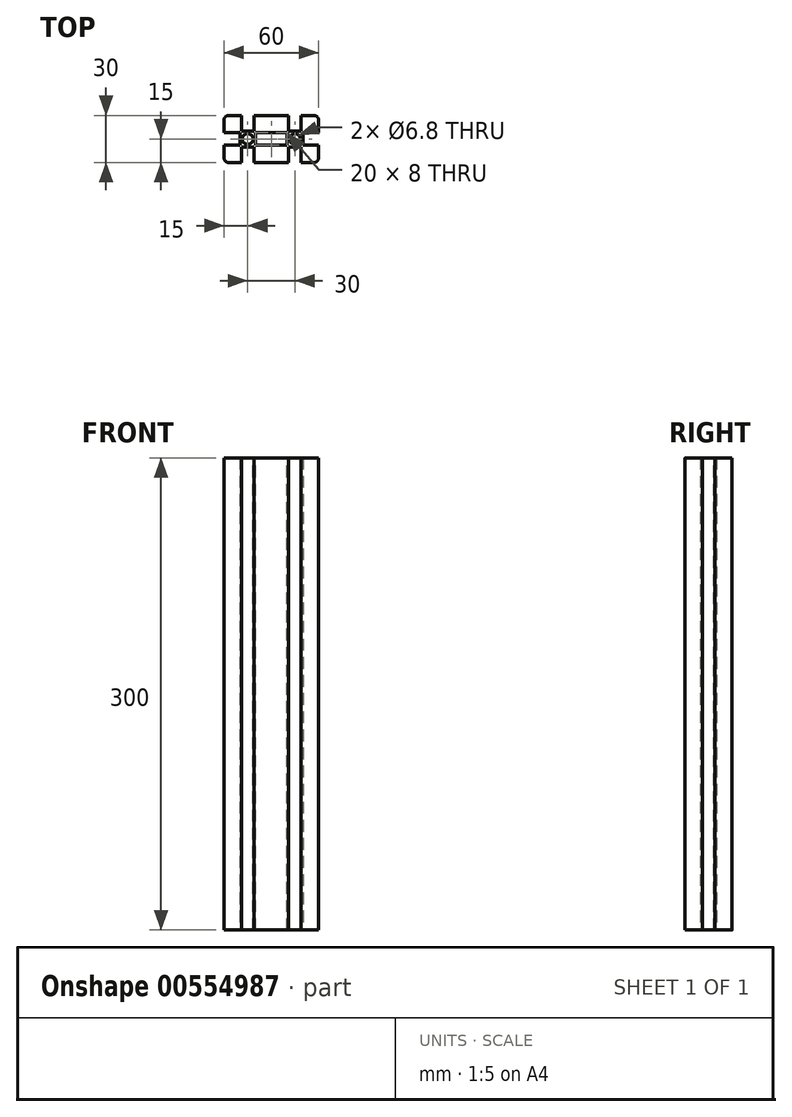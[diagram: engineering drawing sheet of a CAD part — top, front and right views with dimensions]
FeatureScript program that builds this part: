
annotation { "Feature Type Name" : "Feature", "Feature Type Description" : "" }
export const myFeature = defineFeature(function(context is Context, id is Id, definition is map)
    precondition{}
    {
        {
            var Q0;
            Q0=qCreatedBy(makeId("Top.planeOp"),FACE);
            var sketch = newSketch(context, id + "F0", { "sketchPlane" : qUnion([Q0])});
            skLineSegment(sketch, "E0.bottom", {"start": v(30, 15) * mm, "end": v(19, 15) * mm});
            skLineSegment(sketch, "E0.top", {"start": v(30, -15) * mm, "end": v(19, -15) * mm});
            skLineSegment(sketch, "E0.left", {"start": v(30, 15) * mm, "end": v(30, 4) * mm});
            skLineSegment(sketch, "E0.right", {"start": v(-30, 15) * mm, "end": v(-30, 4) * mm});
            skPoint(sketch, "E0.middle", {"position": v(0, 0) * mm});
            skLineSegment(sketch, "E1.bottom", {"start": v(-30, 4) * mm, "end": v(-20, 4) * mm});
            skLineSegment(sketch, "E1.top", {"start": v(-30, -4) * mm, "end": v(-20, -4) * mm});
            skLineSegment(sketch, "E1.right", {"start": v(-20, 4) * mm, "end": v(-20, -4) * mm});
            skLineSegment(sketch, "E2.top", {"start": v(-19, 5) * mm, "end": v(-11, 5) * mm});
            skLineSegment(sketch, "E2.left", {"start": v(-19, 15) * mm, "end": v(-19, 5) * mm});
            skLineSegment(sketch, "E2.right", {"start": v(-11, 15) * mm, "end": v(-11, 5) * mm});
            skLineSegment(sketch, "E3.top", {"start": v(-19, -5) * mm, "end": v(-11, -5) * mm});
            skLineSegment(sketch, "E3.left", {"start": v(-19, -15) * mm, "end": v(-19, -5) * mm});
            skLineSegment(sketch, "E3.right", {"start": v(-11, -15) * mm, "end": v(-11, -5) * mm});
            skLineSegment(sketch, "E4.MirrorCS", {"start": v(11, 15) * mm, "end": v(11, 5) * mm});
            skLineSegment(sketch, "E5.MirrorCS", {"start": v(19, 5) * mm, "end": v(11, 5) * mm});
            skLineSegment(sketch, "E6.MirrorCS", {"start": v(19, 15) * mm, "end": v(19, 5) * mm});
            skLineSegment(sketch, "E7.MirrorCS", {"start": v(30, 4) * mm, "end": v(20, 4) * mm});
            skLineSegment(sketch, "E8.MirrorCS", {"start": v(20, 4) * mm, "end": v(20, -4) * mm});
            skLineSegment(sketch, "E9.MirrorCS", {"start": v(30, -4) * mm, "end": v(20, -4) * mm});
            skLineSegment(sketch, "E10.MirrorCS", {"start": v(11, -15) * mm, "end": v(11, -5) * mm});
            skLineSegment(sketch, "E11.MirrorCS", {"start": v(19, -5) * mm, "end": v(11, -5) * mm});
            skLineSegment(sketch, "E12.MirrorCS", {"start": v(19, -15) * mm, "end": v(19, -5) * mm});
            skLineSegment(sketch, "E13.trimOffspring", {"start": v(-30, -4) * mm, "end": v(-30, -15) * mm});
            skLineSegment(sketch, "E14.trimOffspring", {"start": v(-19, 15) * mm, "end": v(-30, 15) * mm});
            skLineSegment(sketch, "E15.trimOffspring", {"start": v(-19, -15) * mm, "end": v(-30, -15) * mm});
            skLineSegment(sketch, "E16.trimOffspring", {"start": v(11, -15) * mm, "end": v(-11, -15) * mm});
            skLineSegment(sketch, "E17.trimOffspring", {"start": v(30, -4) * mm, "end": v(30, -15) * mm});
            skLineSegment(sketch, "E18.trimOffspring", {"start": v(11, 15) * mm, "end": v(-11, 15) * mm});
            skSolve(sketch);
        }
        {
            var Q0;
            Q0 = qSketchRegion(id + "F0", true);
            extrude(context, id + "F1", {"entities" : qUnion([Q0]), "endBound" : BoundingType.SYMMETRIC, "depth" : 300 * mm, "offsetDistance" : 25 * mm});
        }
        {
            var Q0;
            Q0=makeQuery(id+"F1.opExtrude","CAP_FACE",FACE,{"disambiguationData":[OSD([sQuery(id+"F0.wireOp",EDGE,"E0.bottom"),sQuery(id+"F0.wireOp",EDGE,"E0.top"),sQuery(id+"F0.wireOp",EDGE,"E0.left"),sQuery(id+"F0.wireOp",EDGE,"E0.right"),sQuery(id+"F0.wireOp",EDGE,"E1.bottom"),sQuery(id+"F0.wireOp",EDGE,"E1.top"),sQuery(id+"F0.wireOp",EDGE,"E1.right"),sQuery(id+"F0.wireOp",EDGE,"E2.top"),sQuery(id+"F0.wireOp",EDGE,"E2.left"),sQuery(id+"F0.wireOp",EDGE,"E2.right"),sQuery(id+"F0.wireOp",EDGE,"E3.top"),sQuery(id+"F0.wireOp",EDGE,"E3.left"),sQuery(id+"F0.wireOp",EDGE,"E3.right"),sQuery(id+"F0.wireOp",EDGE,"E4.MirrorCS"),sQuery(id+"F0.wireOp",EDGE,"E5.MirrorCS"),sQuery(id+"F0.wireOp",EDGE,"E6.MirrorCS"),sQuery(id+"F0.wireOp",EDGE,"E7.MirrorCS"),sQuery(id+"F0.wireOp",EDGE,"E8.MirrorCS"),sQuery(id+"F0.wireOp",EDGE,"E9.MirrorCS"),sQuery(id+"F0.wireOp",EDGE,"E10.MirrorCS"),sQuery(id+"F0.wireOp",EDGE,"E11.MirrorCS"),sQuery(id+"F0.wireOp",EDGE,"E12.MirrorCS"),sQuery(id+"F0.wireOp",EDGE,"E13.trimOffspring"),sQuery(id+"F0.wireOp",EDGE,"E14.trimOffspring"),sQuery(id+"F0.wireOp",EDGE,"E15.trimOffspring"),sQuery(id+"F0.wireOp",EDGE,"E16.trimOffspring"),sQuery(id+"F0.wireOp",EDGE,"E17.trimOffspring"),sQuery(id+"F0.wireOp",EDGE,"E18.trimOffspring")])],"isStart":false});
            var sketch = newSketch(context, id + "F2", { "sketchPlane" : qUnion([Q0])});
            skLineSegment(sketch, "E19.bottom", {"start": v(10, 4) * mm, "end": v(-10, 4) * mm});
            skLineSegment(sketch, "E19.top", {"start": v(10, -4) * mm, "end": v(-10, -4) * mm});
            skLineSegment(sketch, "E19.left", {"start": v(10, 4) * mm, "end": v(10, -4) * mm});
            skLineSegment(sketch, "E19.right", {"start": v(-10, 4) * mm, "end": v(-10, -4) * mm});
            skPoint(sketch, "E19.middle", {"position": v(0, 0) * mm});
            skCircle(sketch, "E20", {"center": v(-15, 0) * mm, "radius": 3.4 * mm});
            skCircle(sketch, "E21", {"center": v(15, 0) * mm, "radius": 3.4 * mm});
            skSolve(sketch);
        }
        {
            var Q0;
            Q0 = qSketchRegion(id + "F2", true);
            extrude(context, id + "F3", {"entities" : qUnion([Q0]), "operationType" : NewBodyOperationType.REMOVE, "oppositeDirection" : true, "depth" : 300 * mm, "offsetDistance" : 25 * mm});
        }
        {
            var Q0;
            Q0=makeQuery(id+"F1.opExtrude","SWEPT_EDGE",EDGE,{"disambiguationData":[OSD([sQuery(id+"F0.wireOp",EDGE,"E0.top"),sQuery(id+"F0.wireOp",EDGE,"E17.trimOffspring")])]});
            var Q1;
            Q1=makeQuery(id+"F1.opExtrude","SWEPT_EDGE",EDGE,{"disambiguationData":[OSD([sQuery(id+"F0.wireOp",EDGE,"E0.bottom"),sQuery(id+"F0.wireOp",EDGE,"E0.left")])]});
            var Q2;
            Q2=makeQuery(id+"F1.opExtrude","SWEPT_EDGE",EDGE,{"disambiguationData":[OSD([sQuery(id+"F0.wireOp",EDGE,"E13.trimOffspring"),sQuery(id+"F0.wireOp",EDGE,"E15.trimOffspring")])]});
            var Q3;
            Q3=makeQuery(id+"F1.opExtrude","SWEPT_EDGE",EDGE,{"disambiguationData":[OSD([sQuery(id+"F0.wireOp",EDGE,"E0.right"),sQuery(id+"F0.wireOp",EDGE,"E14.trimOffspring")])]});
            fillet(context, id + "F4", {"entities" : qUnion([Q0, Q1, Q2, Q3]), "radius" : 3 * mm, "tangentPropagation" : true, "allowEdgeOverflow" : false});
        }
    });
